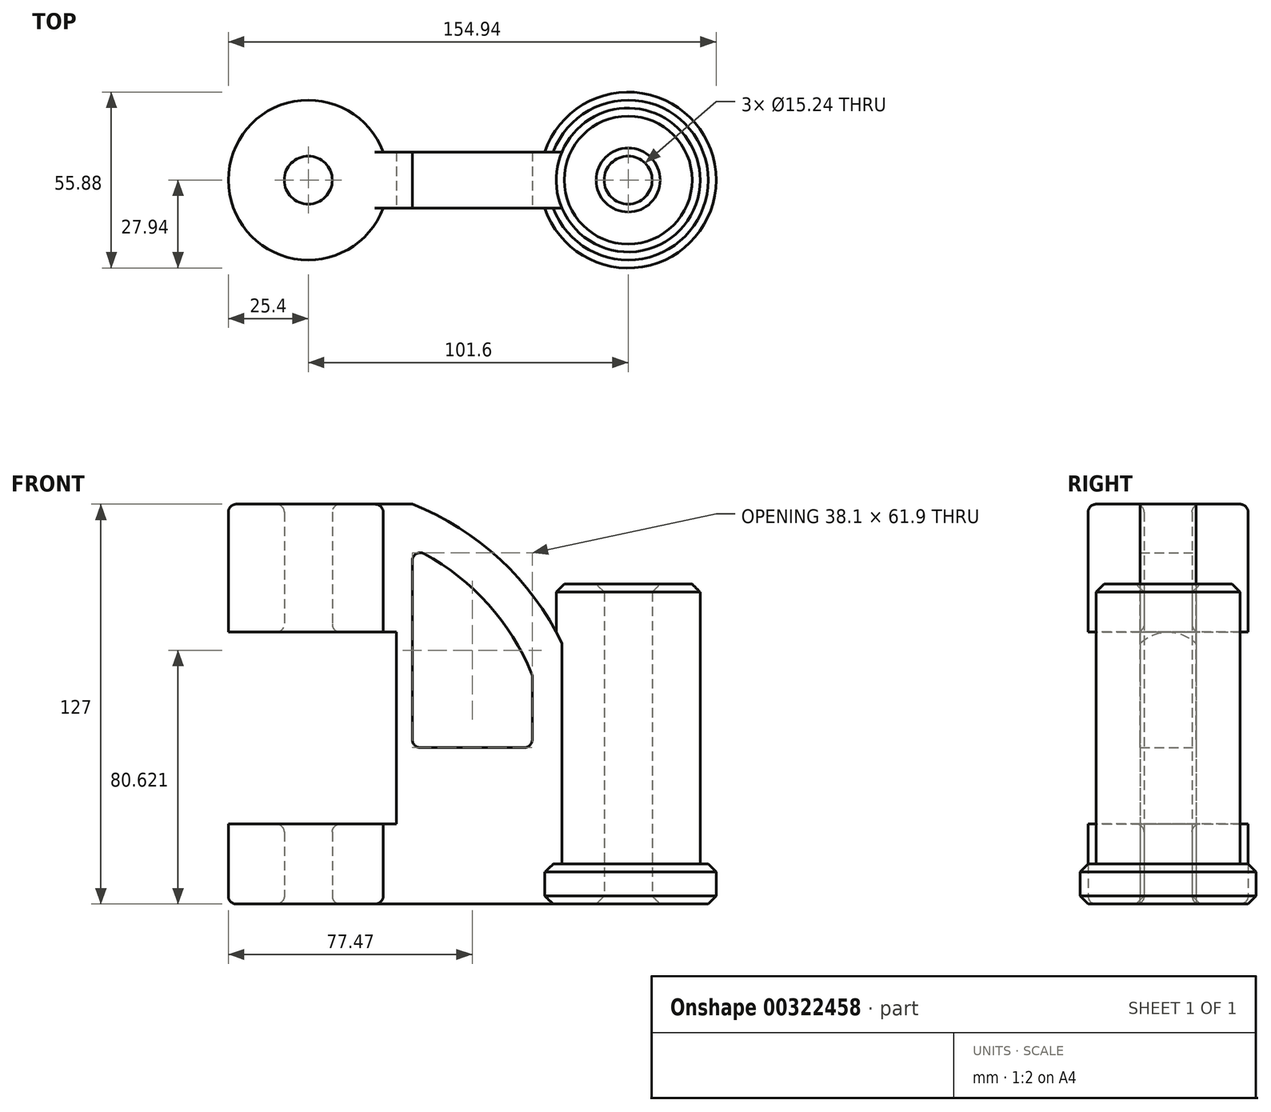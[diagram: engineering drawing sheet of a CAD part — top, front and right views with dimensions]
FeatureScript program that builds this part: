
annotation { "Feature Type Name" : "Feature", "Feature Type Description" : "" }
export const myFeature = defineFeature(function(context is Context, id is Id, definition is map)
    precondition{}
    {
        {
            var Q0;
            Q0=qCreatedBy(makeId("Top.planeOp"),FACE);
            var sketch = newSketch(context, id + "F0", { "sketchPlane" : qUnion([Q0])});
            skCircle(sketch, "E0", {"center": v(0, 0) * mm, "radius": 7.62 * mm});
            skCircle(sketch, "E1", {"center": v(0, 0) * mm, "radius": 25.4 * mm});
            skCircle(sketch, "E2", {"center": v(101.6, 0) * mm, "radius": 7.62 * mm});
            skCircle(sketch, "E3", {"center": v(101.6, 0) * mm, "radius": 22.86 * mm});
            skSolve(sketch);
        }
        {
            var Q0;
            Q0=makeQuery(id+"F0.imprint","IMPRINT",FACE,{"disambiguationData":[TD([[makeQuery(id+"F0.imprint","IMPRINT",EDGE,{"derivedFrom":sQuery(id+"F0.wireOp",EDGE,"E0")}),-1.0]])]});
            extrude(context, id + "F1", {"entities" : qUnion([Q0]), "depth" : 127 * mm});
        }
        {
            var Q0;
            Q0=makeQuery(id+"F0.imprint","IMPRINT",FACE,{"disambiguationData":[TD([[makeQuery(id+"F0.imprint","IMPRINT",EDGE,{"derivedFrom":sQuery(id+"F0.wireOp",EDGE,"E2")}),-1.0]])]});
            extrude(context, id + "F2", {"entities" : qUnion([Q0]), "depth" : 101.6 * mm});
        }
        {
            var Q0;
            Q0=qCreatedBy(makeId("Front.planeOp"),FACE);
            var sketch = newSketch(context, id + "F3", { "sketchPlane" : qUnion([Q0])});
            skLineSegment(sketch, "E4", {"start": v(20.32, 0) * mm, "end": v(20.32, 127) * mm});
            skLineSegment(sketch, "E5", {"start": v(20.32, 127) * mm, "end": v(33.02, 127) * mm});
            skLineSegment(sketch, "E6", {"start": v(20.32, 0) * mm, "end": v(81.28, 0) * mm});
            skLineSegment(sketch, "E7", {"start": v(81.28, 0) * mm, "end": v(81.28, 81.28) * mm});
            skArc(sketch, "E8", {"start": v(81.28, 81.28) * mm, "mid": v(61.58, 108.82) * mm, "end": v(33.02, 127) * mm});
            skLineSegment(sketch, "E9", {"start": v(33.02, 113.17) * mm, "end": v(33.02, 49.67) * mm});
            skLineSegment(sketch, "E10", {"start": v(33.02, 49.67) * mm, "end": v(71.12, 49.67) * mm});
            skLineSegment(sketch, "E11", {"start": v(71.12, 49.67) * mm, "end": v(71.12, 72.77) * mm});
            skArc(sketch, "E12.0", {"start": v(71.12, 72.77) * mm, "mid": v(55.88, 96.56) * mm, "end": v(33.02, 113.17) * mm});
            skSolve(sketch);
        }
        {
            var Q0;
            Q0=makeQuery(id+"F3.imprint","IMPRINT",FACE,{"disambiguationData":[TD([[makeQuery(id+"F3.imprint","IMPRINT",EDGE,{"derivedFrom":sQuery(id+"F3.wireOp",EDGE,"E4")}),-1.0]])]});
            extrude(context, id + "F4", {"entities" : qUnion([Q0]), "operationType" : NewBodyOperationType.ADD, "depth" : 17.78 * mm, "symmetric" : true});
        }
        {
            var Q0;
            Q0=qCreatedBy(makeId("Front.planeOp"),FACE);
            var sketch = newSketch(context, id + "F5", { "sketchPlane" : qUnion([Q0])});
            skLineSegment(sketch, "E13.bottom", {"start": v(-33.02, 86.36) * mm, "end": v(27.94, 86.36) * mm});
            skLineSegment(sketch, "E13.top", {"start": v(-33.02, 25.4) * mm, "end": v(27.94, 25.4) * mm});
            skLineSegment(sketch, "E13.left", {"start": v(-33.02, 86.36) * mm, "end": v(-33.02, 25.4) * mm});
            skLineSegment(sketch, "E13.right", {"start": v(27.94, 86.36) * mm, "end": v(27.94, 25.4) * mm});
            skSolve(sketch);
        }
        {
            var Q0;
            Q0 = qSketchRegion(id + "F5", true);
            extrude(context, id + "F6", {"entities" : qUnion([Q0]), "operationType" : NewBodyOperationType.REMOVE, "oppositeDirection" : true, "depth" : 101.6 * mm, "symmetric" : true});
        }
        {
            var Q0;
            Q0=makeQuery(id+"F4.opExtrude","SWEPT_EDGE",EDGE,{"disambiguationData":[OSD([sQuery(id+"F3.wireOp",EDGE,"E9"),sQuery(id+"F3.wireOp",EDGE,"E12.0")])]});
            var Q1;
            Q1=makeQuery(id+"F4.opExtrude","SWEPT_EDGE",EDGE,{"disambiguationData":[OSD([sQuery(id+"F3.wireOp",EDGE,"E9"),sQuery(id+"F3.wireOp",EDGE,"E10")])]});
            var Q2;
            Q2=makeQuery(id+"F4.opExtrude","SWEPT_EDGE",EDGE,{"disambiguationData":[OSD([sQuery(id+"F3.wireOp",EDGE,"E10"),sQuery(id+"F3.wireOp",EDGE,"E11")])]});
            var Q3;
            Q3=makeQuery(id+"F4.opExtrude","SWEPT_EDGE",EDGE,{"disambiguationData":[OSD([sQuery(id+"F3.wireOp",EDGE,"E11"),sQuery(id+"F3.wireOp",EDGE,"E12.0")])]});
            var Q4;
            Q4=makeQuery(id+"F1.opExtrude","CAP_EDGE",EDGE,{"disambiguationData":[OSD([sQuery(id+"F0.wireOp",EDGE,"E0")])],"isStart":false});
            var Q5;
            Q5=makeQuery(id+"F6.boolean.opBoolean","INTERSECT",EDGE,{"derivedFrom":[makeQuery(id+"F1.opExtrude","SWEPT_FACE",FACE,{"disambiguationData":[OSD([sQuery(id+"F0.wireOp",EDGE,"E0")])]}),makeQuery(id+"F6.opExtrude","SWEPT_FACE",FACE,{"disambiguationData":[OSD([sQuery(id+"F5.wireOp",EDGE,"E13.top")])]})]});
            var Q6;
            Q6=makeQuery(id+"F1.opExtrude","CAP_EDGE",EDGE,{"disambiguationData":[OSD([sQuery(id+"F0.wireOp",EDGE,"E1")])],"isStart":false});
            var Q7;
            Q7=makeQuery(id+"F6.boolean.opBoolean","INTERSECT",EDGE,{"derivedFrom":[makeQuery(id+"F1.opExtrude","SWEPT_FACE",FACE,{"disambiguationData":[OSD([sQuery(id+"F0.wireOp",EDGE,"E0")])]}),makeQuery(id+"F6.opExtrude","SWEPT_FACE",FACE,{"disambiguationData":[OSD([sQuery(id+"F5.wireOp",EDGE,"E13.bottom")])]})]});
            var Q8;
            Q8=makeQuery(id+"F1.opExtrude","CAP_EDGE",EDGE,{"disambiguationData":[OSD([sQuery(id+"F0.wireOp",EDGE,"E0")])],"isStart":true});
            var Q9;
            Q9=makeQuery(id+"F1.opExtrude","CAP_EDGE",EDGE,{"disambiguationData":[OSD([sQuery(id+"F0.wireOp",EDGE,"E1")])],"isStart":true});
            fillet(context, id + "F7", {"entities" : qUnion([Q0, Q1, Q2, Q3, Q4, Q5, Q6, Q7, Q8, Q9]), "radius" : 2.54 * mm, "tangentPropagation" : true, "allowEdgeOverflow" : false});
        }
        {
            var Q0;
            Q0=qCreatedBy(makeId("Top.planeOp"),FACE);
            var sketch = newSketch(context, id + "F8", { "sketchPlane" : qUnion([Q0])});
            skCircle(sketch, "E14.0", {"center": v(101.6, 0) * mm, "radius": 22.86 * mm});
            skCircle(sketch, "E15.0", {"center": v(101.6, 0) * mm, "radius": 27.94 * mm});
            skSolve(sketch);
        }
        {
            var Q0;
            Q0=makeQuery(id+"F8.imprint","IMPRINT",FACE,{"disambiguationData":[TD([[makeQuery(id+"F8.imprint","IMPRINT",EDGE,{"derivedFrom":sQuery(id+"F8.wireOp",EDGE,"E14.0")}),-1.0]])]});
            extrude(context, id + "F9", {"entities" : qUnion([Q0]), "operationType" : NewBodyOperationType.ADD, "depth" : 12.7 * mm});
        }
        {
            var Q0;
            Q0=makeQuery(id+"F9.opExtrude","CAP_EDGE",EDGE,{"disambiguationData":[OSD([sQuery(id+"F8.wireOp",EDGE,"E15.0")])],"isStart":true});
            var Q1;
            Q1=makeQuery(id+"F2.opExtrude","CAP_EDGE",EDGE,{"disambiguationData":[OSD([sQuery(id+"F0.wireOp",EDGE,"E2")])],"isStart":false});
            var Q2;
            Q2=makeQuery(id+"F2.opExtrude","CAP_EDGE",EDGE,{"disambiguationData":[OSD([sQuery(id+"F0.wireOp",EDGE,"E2")])],"isStart":true});
            var Q3;
            Q3=makeQuery(id+"F2.opExtrude","CAP_EDGE",EDGE,{"disambiguationData":[OSD([sQuery(id+"F0.wireOp",EDGE,"E3")])],"isStart":false});
            var Q4;
            Q4=makeQuery(id+"F9.opExtrude","CAP_EDGE",EDGE,{"disambiguationData":[OSD([sQuery(id+"F8.wireOp",EDGE,"E15.0")])],"isStart":false});
            chamfer(context, id + "F10", {"entities" : qUnion([Q0, Q1, Q2, Q3, Q4]), "width" : 2.54 * mm, "tangentPropagation" : true});
        }
    });
